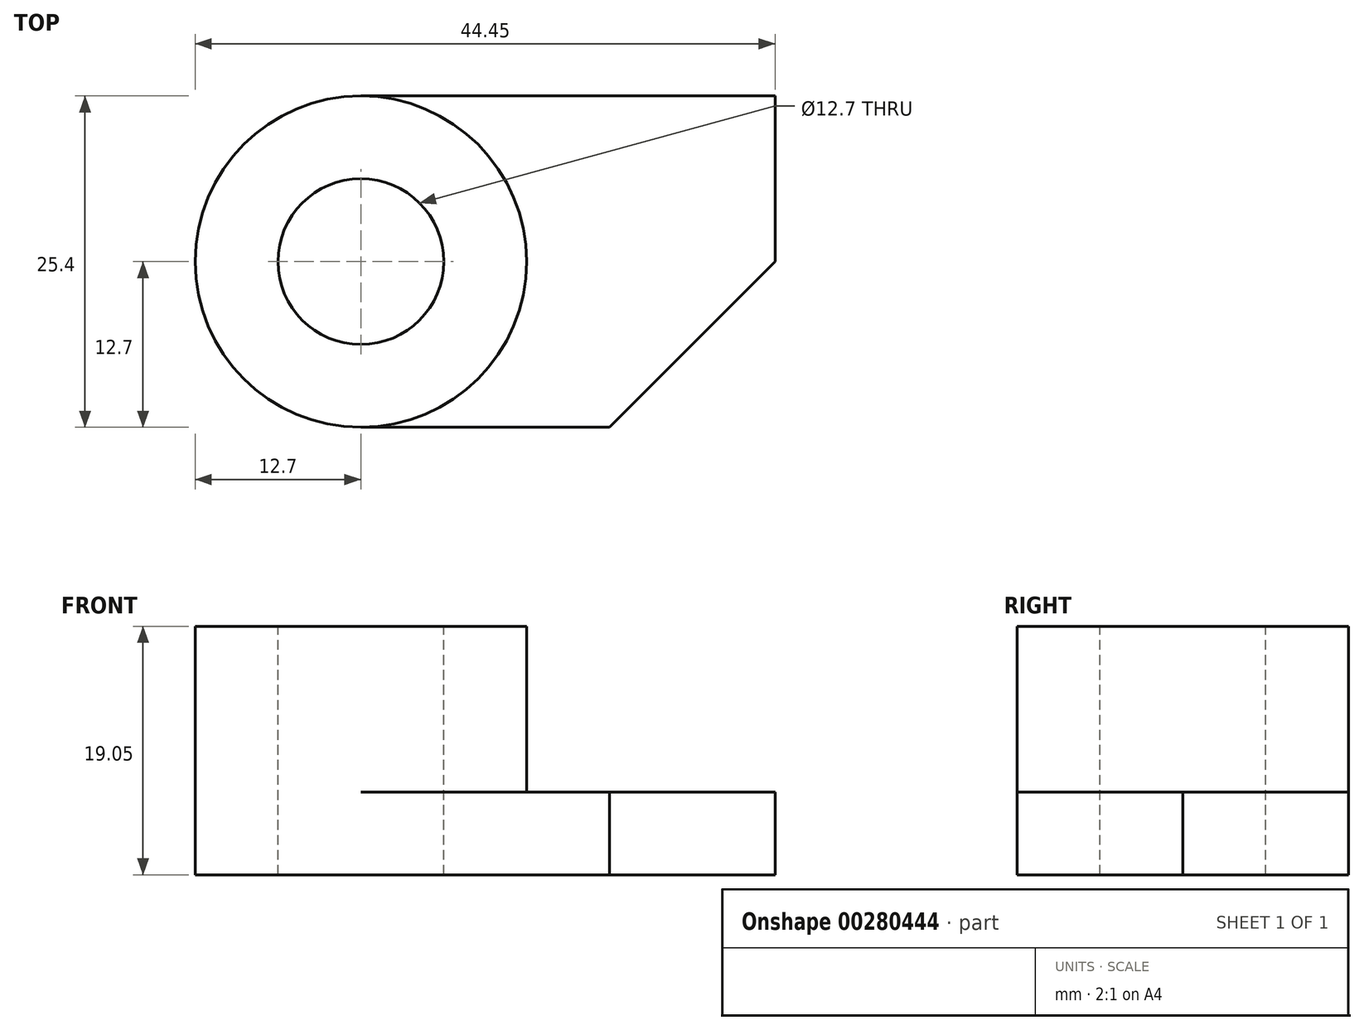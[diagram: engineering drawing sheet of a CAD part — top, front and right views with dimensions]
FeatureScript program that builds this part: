
annotation { "Feature Type Name" : "Feature", "Feature Type Description" : "" }
export const myFeature = defineFeature(function(context is Context, id is Id, definition is map)
    precondition{}
    {
        {
            var Q0;
            Q0=qCreatedBy(makeId("Top.planeOp"),FACE);
            var sketch = newSketch(context, id + "F0", { "sketchPlane" : qUnion([Q0])});
            skCircle(sketch, "E0", {"center": v(0, 0) * mm, "radius": 12.7 * mm});
            skLineSegment(sketch, "E1", {"start": v(0, -12.7) * mm, "end": v(31.75, -12.7) * mm});
            skLineSegment(sketch, "E2", {"start": v(31.75, -12.7) * mm, "end": v(31.75, 12.7) * mm});
            skLineSegment(sketch, "E3", {"start": v(31.75, 12.7) * mm, "end": v(0, 12.7) * mm});
            skSolve(sketch);
        }
        {
            var Q0;
            Q0 = qSketchRegion(id + "F0", true);
            extrude(context, id + "F1", {"entities" : qUnion([Q0]), "oppositeDirection" : true, "depth" : 19.05 * mm});
        }
        {
            var Q0;
            Q0=qCreatedBy(makeId("Top.planeOp"),FACE);
            var sketch = newSketch(context, id + "F2", { "sketchPlane" : qUnion([Q0])});
            skLineSegment(sketch, "E4", {"start": v(19.05, -12.7) * mm, "end": v(31.75, 0) * mm});
            skLineSegment(sketch, "E5", {"start": v(31.75, 0) * mm, "end": v(31.75, -12.7) * mm});
            skLineSegment(sketch, "E6", {"start": v(31.75, -12.7) * mm, "end": v(19.05, -12.7) * mm});
            skSolve(sketch);
        }
        {
            var Q0;
            Q0 = qSketchRegion(id + "F2", true);
            extrude(context, id + "F3", {"entities" : qUnion([Q0]), "operationType" : NewBodyOperationType.REMOVE, "oppositeDirection" : true, "depth" : 25.4 * mm});
        }
        {
            var Q0;
            Q0=qCreatedBy(makeId("Top.planeOp"),FACE);
            var sketch = newSketch(context, id + "F4", { "sketchPlane" : qUnion([Q0])});
            skCircle(sketch, "E7", {"center": v(0, 0) * mm, "radius": 6.35 * mm});
            skSolve(sketch);
        }
        {
            var Q0;
            Q0 = qSketchRegion(id + "F4", true);
            extrude(context, id + "F5", {"entities" : qUnion([Q0]), "operationType" : NewBodyOperationType.REMOVE, "oppositeDirection" : true, "depth" : 25.4 * mm});
        }
        {
            var Q0;
            Q0=qCreatedBy(makeId("Top.planeOp"),FACE);
            var sketch = newSketch(context, id + "F6", { "sketchPlane" : qUnion([Q0])});
            skLineSegment(sketch, "E8", {"start": v(0, 12.7) * mm, "end": v(36.23, 12.7) * mm});
            skLineSegment(sketch, "E9", {"start": v(36.23, 12.7) * mm, "end": v(36.23, -12.7) * mm});
            skLineSegment(sketch, "E10", {"start": v(36.23, -12.7) * mm, "end": v(0, -12.7) * mm});
            skArc(sketch, "E11", {"start": v(0, -12.7) * mm, "mid": v(12.7, 0) * mm, "end": v(0, 12.7) * mm});
            skSolve(sketch);
        }
        {
            var Q0;
            Q0 = qSketchRegion(id + "F6", true);
            extrude(context, id + "F7", {"entities" : qUnion([Q0]), "operationType" : NewBodyOperationType.REMOVE, "oppositeDirection" : true, "depth" : 12.7 * mm});
        }
    });
